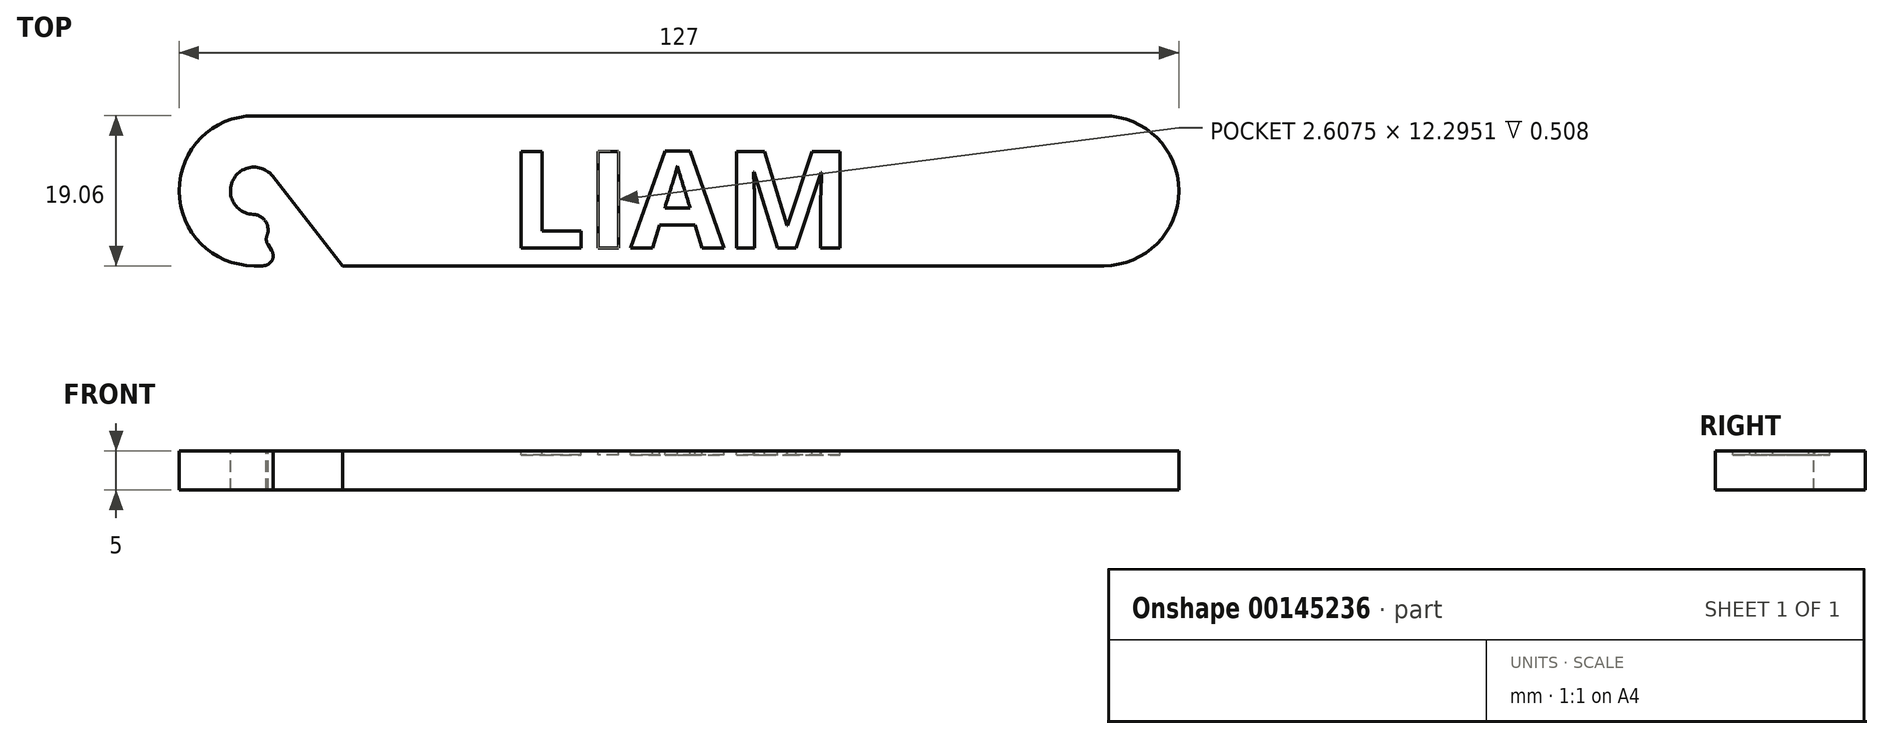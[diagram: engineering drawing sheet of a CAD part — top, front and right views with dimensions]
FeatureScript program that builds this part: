
annotation { "Feature Type Name" : "Feature", "Feature Type Description" : "" }
export const myFeature = defineFeature(function(context is Context, id is Id, definition is map)
    precondition{}
    {
        {
            var Q0;
            Q0=qCreatedBy(makeId("Top.planeOp"),FACE);
            var sketch = newSketch(context, id + "F0", { "sketchPlane" : qUnion([Q0])});
            skLineSegment(sketch, "E0.bottom", {"start": v(63.5, -9.52) * mm, "end": v(-63.5, -9.53) * mm});
            skLineSegment(sketch, "E0.top", {"start": v(63.5, 9.53) * mm, "end": v(-63.5, 9.52) * mm});
            skLineSegment(sketch, "E0.left", {"start": v(63.5, -9.52) * mm, "end": v(63.5, 9.53) * mm});
            skLineSegment(sketch, "E0.right", {"start": v(-63.5, -9.53) * mm, "end": v(-63.5, 9.52) * mm});
            skPoint(sketch, "E0.middle", {"position": v(0, 0) * mm});
            skSolve(sketch);
        }
        {
            var Q0;
            Q0=makeQuery(id+"F0.imprint","IMPRINT",FACE,{"disambiguationData":[TD([[makeQuery(id+"F0.imprint","IMPRINT",EDGE,{"derivedFrom":sQuery(id+"F0.wireOp",EDGE,"E0.bottom")}),-1.0]])]});
            extrude(context, id + "F1", {"entities" : qUnion([Q0]), "depth" : 5 * mm});
        }
        {
            var Q0;
            Q0=makeQuery(id+"F1.opExtrude","SWEPT_EDGE",EDGE,{"disambiguationData":[OSD([sQuery(id+"F0.wireOp",EDGE,"E0.bottom"),sQuery(id+"F0.wireOp",EDGE,"E0.right")])]});
            var Q1;
            Q1=makeQuery(id+"F1.opExtrude","SWEPT_EDGE",EDGE,{"disambiguationData":[OSD([sQuery(id+"F0.wireOp",EDGE,"E0.top"),sQuery(id+"F0.wireOp",EDGE,"E0.right")])]});
            var Q2;
            Q2=makeQuery(id+"F1.opExtrude","SWEPT_EDGE",EDGE,{"disambiguationData":[OSD([sQuery(id+"F0.wireOp",EDGE,"E0.bottom"),sQuery(id+"F0.wireOp",EDGE,"E0.left")])]});
            var Q3;
            Q3=makeQuery(id+"F1.opExtrude","SWEPT_EDGE",EDGE,{"disambiguationData":[OSD([sQuery(id+"F0.wireOp",EDGE,"E0.top"),sQuery(id+"F0.wireOp",EDGE,"E0.left")])]});
            fillet(context, id + "F2", {"entities" : qUnion([Q0, Q1, Q2, Q3]), "radius" : 9.52 * mm, "tangentPropagation" : true, "allowEdgeOverflow" : false});
        }
        {
            var Q0;
            Q0=makeQuery(id+"F1.opExtrude","CAP_FACE",FACE,{"disambiguationData":[OSD([sQuery(id+"F0.wireOp",EDGE,"E0.bottom"),sQuery(id+"F0.wireOp",EDGE,"E0.top"),sQuery(id+"F0.wireOp",EDGE,"E0.left"),sQuery(id+"F0.wireOp",EDGE,"E0.right")])],"isStart":false});
            var sketch = newSketch(context, id + "F3", { "sketchPlane" : qUnion([Q0])});
            skCircle(sketch, "E1", {"center": v(-53.98, 0) * mm, "radius": 3 * mm});
            skSolve(sketch);
        }
        {
            var Q0;
            Q0=makeQuery(id+"F3.imprint","IMPRINT",FACE,{"disambiguationData":[TD([[makeQuery(id+"F3.imprint","IMPRINT",EDGE,{"derivedFrom":sQuery(id+"F3.wireOp",EDGE,"E1")}),1.0]])]});
            extrude(context, id + "F4", {"entities" : qUnion([Q0]), "operationType" : NewBodyOperationType.REMOVE, "endBound" : BoundingType.THROUGH_ALL, "oppositeDirection" : true, "depth" : 25.4 * mm});
        }
        {
            var Q0;
            Q0=makeQuery(id+"F1.opExtrude","CAP_FACE",FACE,{"disambiguationData":[OSD([sQuery(id+"F0.wireOp",EDGE,"E0.bottom"),sQuery(id+"F0.wireOp",EDGE,"E0.top"),sQuery(id+"F0.wireOp",EDGE,"E0.left"),sQuery(id+"F0.wireOp",EDGE,"E0.right")])],"isStart":false});
            var sketch = newSketch(context, id + "F5", { "sketchPlane" : qUnion([Q0])});
            skLineSegment(sketch, "E2", {"start": v(-51.6, 1.85) * mm, "end": v(-42.74, -9.53) * mm});
            skArc(sketch, "E3", {"start": v(-52.63, -6.2) * mm, "mid": v(-52.37, -4.15) * mm, "end": v(-54.1, -3) * mm});
            skLineSegment(sketch, "E4.trimOffspring", {"start": v(-52.63, -6.2) * mm, "end": v(-50.48, -9.53) * mm});
            skPoint(sketch, "E5.start.orphan", {"position": v(-54.77, -2.9) * mm});
            skSolve(sketch);
        }
        {
            var Q0;
            {var subQ1=sQuery(id+"F5.wireOp",EDGE,"E2");Q0=makeQuery(id+"F5.imprint","IMPRINT",FACE,{"disambiguationData":[TD([[makeQuery(id+"F5.imprint","IMPRINT",EDGE,{"derivedFrom":subQ1}),-1.0]])]});}
            extrude(context, id + "F6", {"entities" : qUnion([Q0]), "operationType" : NewBodyOperationType.REMOVE, "endBound" : BoundingType.THROUGH_ALL, "oppositeDirection" : true, "depth" : 25.4 * mm});
        }
        {
            var Q0;
            Q0=makeQuery(id+"F6.boolean.opBoolean","COPY",EDGE,{"derivedFrom":makeQuery(id+"F6.opExtrude","SWEPT_EDGE",EDGE,{"disambiguationData":[OSD([sQuery(id+"F5.wireOp",EDGE,"E3"),sQuery(id+"F5.wireOp",EDGE,"E4.trimOffspring")])]})});
            var Q1;
            Q1=makeQuery(id+"F6.boolean.opBoolean","COPY",EDGE,{"derivedFrom":makeQuery(id+"F6.opExtrude","SWEPT_EDGE",EDGE,{"disambiguationData":[OSD([sQuery(id+"F0.wireOp",EDGE,"E0.bottom"),sQuery(id+"F5.wireOp",EDGE,"E4.trimOffspring")])]})});
            var Q2;
            Q2=makeQuery(id+"Fjk8D6rC3UBreEa_1.1.F6.boolean.opBoolean","COPY",EDGE,{"derivedFrom":makeQuery(id+"Fjk8D6rC3UBreEa_1.1.F6.opExtrude","SWEPT_EDGE",EDGE,{"disambiguationData":[OSD([sQuery(id+"F5.wireOp",EDGE,"E3"),sQuery(id+"F5.wireOp",EDGE,"E4.trimOffspring")])]})});
            var Q3;
            Q3=makeQuery(id+"Fjk8D6rC3UBreEa_1.1.F6.boolean.opBoolean","COPY",EDGE,{"derivedFrom":makeQuery(id+"Fjk8D6rC3UBreEa_1.1.F6.opExtrude","SWEPT_EDGE",EDGE,{"disambiguationData":[OSD([sQuery(id+"F0.wireOp",EDGE,"E0.bottom"),sQuery(id+"F5.wireOp",EDGE,"E4.trimOffspring")])]})});
            fillet(context, id + "F7", {"entities" : qUnion([Q0, Q1, Q2, Q3]), "radius" : 1.27 * mm, "tangentPropagation" : true, "allowEdgeOverflow" : false});
        }
        {
            var Q0;
            Q0=makeQuery(id+"F1.opExtrude","CAP_FACE",FACE,{"disambiguationData":[OSD([sQuery(id+"F0.wireOp",EDGE,"E0.bottom"),sQuery(id+"F0.wireOp",EDGE,"E0.top"),sQuery(id+"F0.wireOp",EDGE,"E0.left"),sQuery(id+"F0.wireOp",EDGE,"E0.right")])],"isStart":false});
            var sketch = newSketch(context, id + "F8", { "sketchPlane" : qUnion([Q0])});
            skText(sketch, "E6", { "text": "LIAM", "fontName": "OpenSans-Bold.ttf"});
            skPoint(sketch, "E7", {"position": v(0, 5.13) * mm});
            const initialGuessF8  = {"E6": [-0.02157, -0.00728, 1, 0, 0.0124]};
            skSetInitialGuess(sketch, initialGuessF8);
            skSolve(sketch);
        }
        {
            var Q0;
            Q0 = qSketchRegion(id + "F8", true);
            extrude(context, id + "F9", {"entities" : qUnion([Q0]), "operationType" : NewBodyOperationType.REMOVE, "oppositeDirection" : true, "depth" : 0.5 * mm});
        }
    });
